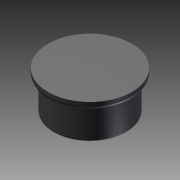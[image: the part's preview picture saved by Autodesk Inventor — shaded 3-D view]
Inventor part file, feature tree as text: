
AUTODESK INVENTOR PART (.ipt)
format: ipt  version: 2014 (Build 180170000, 170)  size: 122,368 bytes
history: native  units: in
note: dims shown in document units (in); Inventor stores cm internally (conversion verified against a paired STEP export)
features: other x14, revolve x2, sketch x2
ambient origin geometry x8: Origin, YZ Plane, XZ Plane, XY Plane, X Axis, Y Axis, Z Axis, Center Point
bodies: Solid1 (feature_tree)
feature tree (18):
  revolve  "Revolution1"  Angle=360.0deg
  revolve  "Revolution2"  [1 undecoded]
  other  "to_body_XY"
  other  "to_body_YZ"
  other  "to_body_ZX"
  other  "to_body_X"
  other  "to_body_Y"
  other  "to_body_Z"
  other  "to_body_Center"
  other  "to_trmnls_XY"
  other  "to_trmnls_YZ"
  other  "to_trmnls_ZX"
  other  "to_trmnls_X"
  other  "to_trmnls_Y"
  other  "to_trmnls_Z"
  other  "to_trmnls_Center"
  sketch  "Sketch_2"  dims[d0=360.0deg d1=360.0deg]
  sketch  "Sketch_4"
note: 1 required parameter value undecoded (feature->parameter linkage not recoverable at this tier; creation-order binding heuristic only, values carry confidence <= 0.55)
